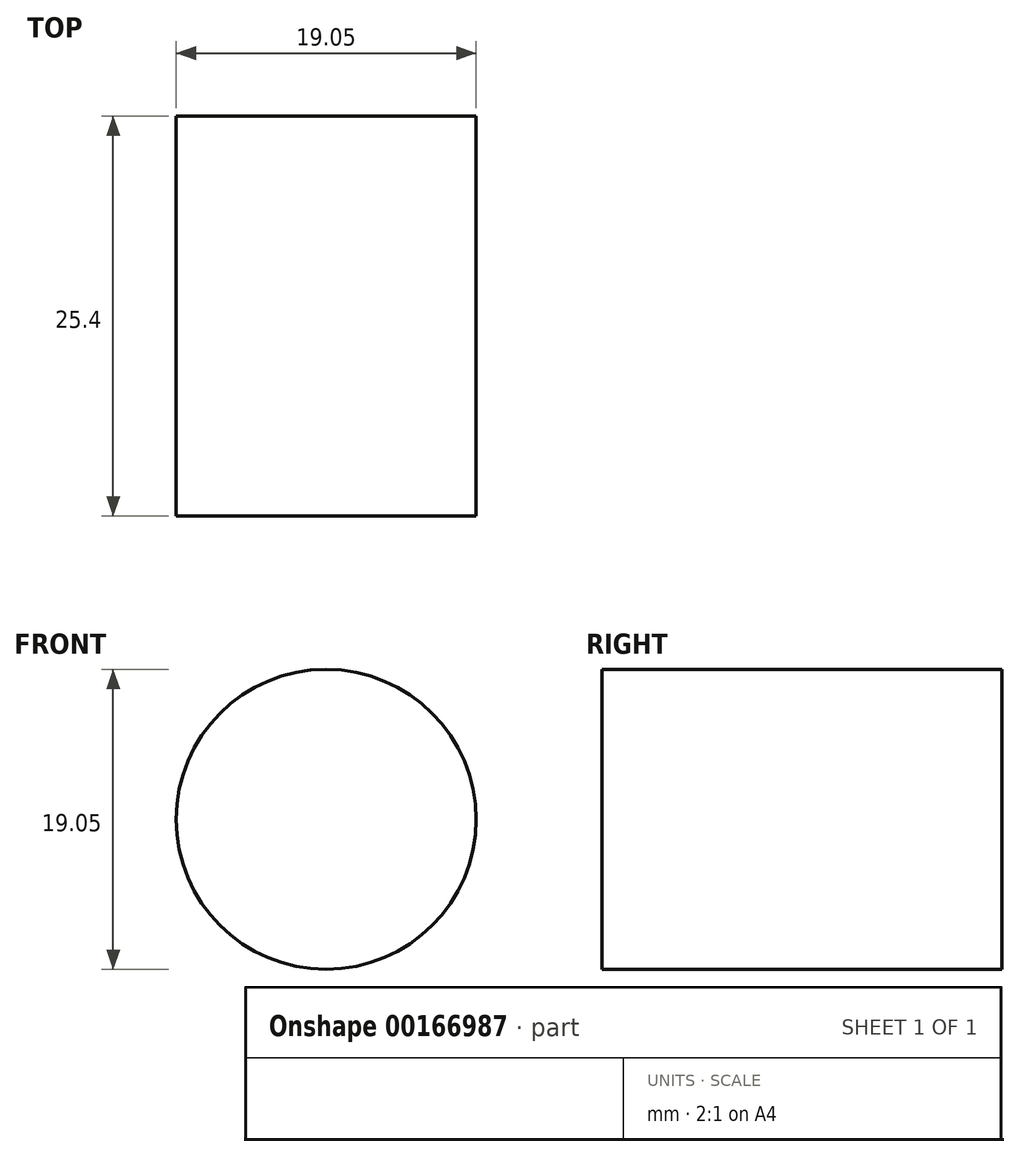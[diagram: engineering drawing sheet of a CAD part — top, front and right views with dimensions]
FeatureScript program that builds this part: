
annotation { "Feature Type Name" : "Feature", "Feature Type Description" : "" }
export const myFeature = defineFeature(function(context is Context, id is Id, definition is map)
    precondition{}
    {
        {
            var Q0;
            Q0=qCreatedBy(makeId("Front.planeOp"),FACE);
            var sketch = newSketch(context, id + "F0", { "sketchPlane" : qUnion([Q0])});
            skCircle(sketch, "E0", {"center": v(-0.2, -0.28) * mm, "radius": 9.53 * mm});
            skSolve(sketch);
        }
        {
            var Q0;
            Q0 = qSketchRegion(id + "F0", true);
            extrude(context, id + "F1", {"entities" : qUnion([Q0]), "depth" : 25.4 * mm});
        }
    });
